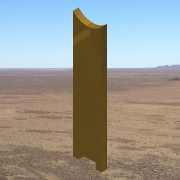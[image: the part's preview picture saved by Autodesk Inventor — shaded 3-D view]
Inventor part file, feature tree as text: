
AUTODESK INVENTOR PART (.ipt)
format: ipt  version: 2013 SP2 (Build 170200200, 200)  size: 141,312 bytes
history: native  units: in
note: dims shown in document units (in); Inventor stores cm internally (conversion verified against a paired STEP export)
features: extrude x3, sketch x3
ambient origin geometry x8: Origin, YZ Plane, XZ Plane, XY Plane, X Axis, Y Axis, Z Axis, Center Point
bodies: Solid1 (feature_tree)
feature tree (6):
  extrude  "Extrusion1"  Depth=0.625in
  extrude  "Extrusion2"  Depth=0.375in
  extrude  "Extrusion3"  TaperAngle=0.0deg  [1 undecoded]
  sketch  "Sketch1"  dims[d0=3.06in d1=0.625in]
  sketch  "Sketch2"  dims[d2=0.125in d3=0.0in d4=0.375in]
  sketch  "Sketch3"  dims[d6=0.125in d7=0.0in d8=0.0in d9=0.125in d10=0.0in d11=0.845in]
note: 1 required parameter value undecoded (feature->parameter linkage not recoverable at this tier; creation-order binding heuristic only, values carry confidence <= 0.55)
